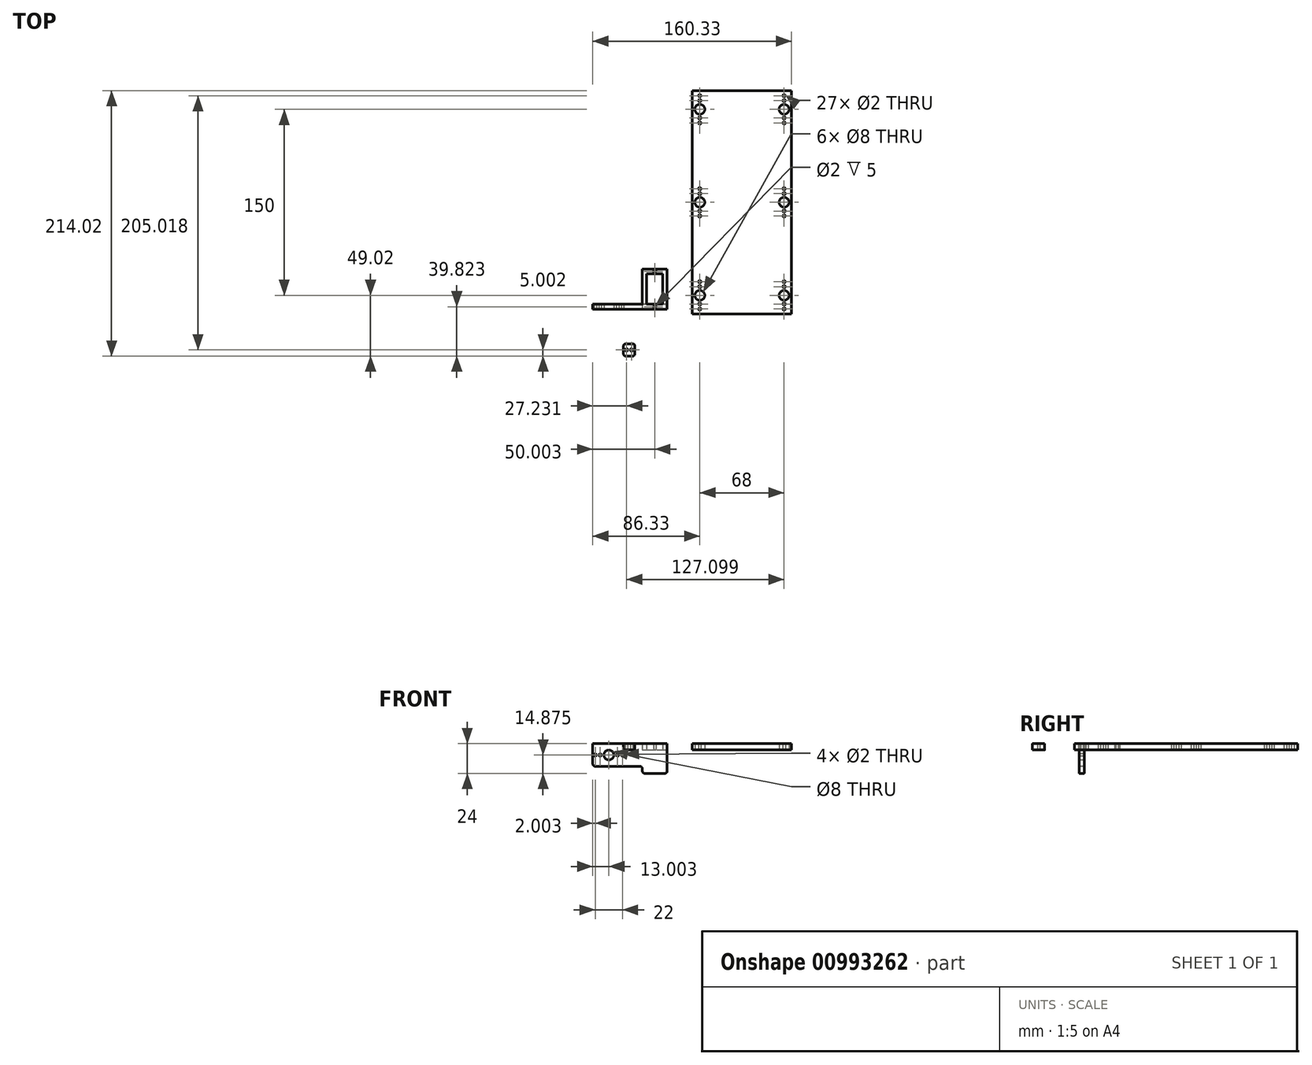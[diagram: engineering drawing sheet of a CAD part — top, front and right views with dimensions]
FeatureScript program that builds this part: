
annotation { "Feature Type Name" : "Feature", "Feature Type Description" : "" }
export const myFeature = defineFeature(function(context is Context, id is Id, definition is map)
    precondition{}
    {
        {
            var Q0;
            Q0=qCreatedBy(makeId("Top.planeOp"),FACE);
            var sketch = newSketch(context, id + "F0", { "sketchPlane" : qUnion([Q0])});
            skLineSegment(sketch, "E0.bottom", {"start": v(-36.83, 32.3) * mm, "end": v(-23.83, 32.3) * mm});
            skLineSegment(sketch, "E0.top", {"start": v(-36.83, 7.8) * mm, "end": v(-23.83, 7.8) * mm});
            skLineSegment(sketch, "E0.left", {"start": v(-36.83, 32.3) * mm, "end": v(-36.83, 7.8) * mm});
            skLineSegment(sketch, "E0.right", {"start": v(-23.83, 32.3) * mm, "end": v(-23.83, 7.8) * mm});
            skLineSegment(sketch, "E1.bottom", {"start": v(-40.33, 36.3) * mm, "end": v(-20.33, 36.3) * mm});
            skLineSegment(sketch, "E1.top", {"start": v(-40.33, 3.8) * mm, "end": v(-20.33, 3.8) * mm});
            skLineSegment(sketch, "E1.left", {"start": v(-40.33, 36.3) * mm, "end": v(-40.33, 3.8) * mm});
            skLineSegment(sketch, "E1.right", {"start": v(-20.33, 36.3) * mm, "end": v(-20.33, 3.8) * mm});
            skCircle(sketch, "E2", {"center": v(-30.33, 34.3) * mm, "radius": 1 * mm});
            skCircle(sketch, "E3", {"center": v(-30.33, 5.8) * mm, "radius": 1 * mm});
            skSolve(sketch);
        }
        {
            var Q0;
            Q0=makeQuery(id+"F0.imprint","IMPRINT",FACE,{"disambiguationData":[TD([[makeQuery(id+"F0.imprint","IMPRINT",EDGE,{"derivedFrom":sQuery(id+"F0.wireOp",EDGE,"E0.bottom")}),1.0]])]});
            extrude(context, id + "F1", {"entities" : qUnion([Q0]), "depth" : 5 * mm, "offsetDistance" : 25 * mm});
        }
        {
            var Q0;
            Q0=makeQuery(id+"F1.opExtrude","SWEPT_FACE",FACE,{"disambiguationData":[OSD([sQuery(id+"F0.wireOp",EDGE,"E1.top")])]});
            var sketch = newSketch(context, id + "F2", { "sketchPlane" : qUnion([Q0])});
            skLineSegment(sketch, "E4.bottom", {"start": v(-40.33, 0) * mm, "end": v(-20.33, 0) * mm});
            skLineSegment(sketch, "E4.top", {"start": v(-40.33, -19) * mm, "end": v(-20.33, -19) * mm});
            skLineSegment(sketch, "E4.left", {"start": v(-40.33, 5) * mm, "end": v(-40.33, 0) * mm});
            skLineSegment(sketch, "E4.right", {"start": v(-20.33, 0) * mm, "end": v(-20.33, -19) * mm});
            skLineSegment(sketch, "E5.bottom", {"start": v(-40.33, 5) * mm, "end": v(-80.33, 5) * mm});
            skLineSegment(sketch, "E5.top", {"start": v(-40.33, -13.25) * mm, "end": v(-80.33, -13.25) * mm});
            skLineSegment(sketch, "E5.right", {"start": v(-80.33, 5) * mm, "end": v(-80.33, -13.25) * mm});
            skLineSegment(sketch, "E6.trimOffspring", {"start": v(-40.33, -13.25) * mm, "end": v(-40.33, -19) * mm});
            skCircle(sketch, "E7", {"center": v(-78.33, -4.13) * mm, "radius": 1 * mm});
            skCircle(sketch, "E8", {"center": v(-74.33, -4.13) * mm, "radius": 1 * mm});
            skCircle(sketch, "E9", {"center": v(-67.33, -4.13) * mm, "radius": 4 * mm});
            skCircle(sketch, "E10", {"center": v(-60.33, -4.13) * mm, "radius": 1 * mm});
            skCircle(sketch, "E11", {"center": v(-56.33, -4.13) * mm, "radius": 1 * mm});
            skSolve(sketch);
        }
        {
            var Q0;
            Q0=makeQuery(id+"F2.imprint","IMPRINT",FACE,{"disambiguationData":[TD([[makeQuery(id+"F2.imprint","IMPRINT",EDGE,{"derivedFrom":sQuery(id+"F2.wireOp",EDGE,"E4.bottom")}),-1.0]])]});
            extrude(context, id + "F3", {"entities" : qUnion([Q0]), "operationType" : NewBodyOperationType.ADD, "oppositeDirection" : true, "depth" : 4 * mm, "offsetDistance" : 25 * mm});
        }
        {
            var Q0;
            Q0=makeQuery(id+"F3.opExtrude","SWEPT_EDGE",EDGE,{"disambiguationData":[OSD([sQuery(id+"F2.wireOp",EDGE,"E4.left"),sQuery(id+"F2.wireOp",EDGE,"E5.bottom")])]});
            var Q1;
            Q1=makeQuery(id+"F3.opExtrude","SWEPT_EDGE",EDGE,{"disambiguationData":[OSD([sQuery(id+"F2.wireOp",EDGE,"E5.top"),sQuery(id+"F2.wireOp",EDGE,"E6.trimOffspring")])]});
            var Q2;
            Q2=makeQuery(id+"F3.opExtrude","SWEPT_EDGE",EDGE,{"disambiguationData":[OSD([sQuery(id+"F2.wireOp",EDGE,"E4.top"),sQuery(id+"F2.wireOp",EDGE,"E6.trimOffspring")])]});
            var Q3;
            Q3=makeQuery(id+"F3.opExtrude","SWEPT_EDGE",EDGE,{"disambiguationData":[OSD([sQuery(id+"F2.wireOp",EDGE,"E4.top"),sQuery(id+"F2.wireOp",EDGE,"E4.right")])]});
            var Q4;
            Q4=makeQuery(id+"F3.opExtrude","SWEPT_EDGE",EDGE,{"disambiguationData":[OSD([sQuery(id+"F2.wireOp",EDGE,"E5.top"),sQuery(id+"F2.wireOp",EDGE,"E5.right")])]});
            fillet(context, id + "F4", {"entities" : qUnion([Q0, Q1, Q2, Q3, Q4]), "radius" : 2 * mm, "tangentPropagation" : true, "allowEdgeOverflow" : false});
        }
        {
            var Q0;
            Q0=qCreatedBy(makeId("Top.planeOp"),FACE);
            var sketch = newSketch(context, id + "F5", { "sketchPlane" : qUnion([Q0])});
            skLineSegment(sketch, "E12.bottom", {"start": v(-55.6, -24.02) * mm, "end": v(-46.34, -24.02) * mm});
            skLineSegment(sketch, "E12.top", {"start": v(-55.6, -34.02) * mm, "end": v(-46.34, -34.02) * mm});
            skLineSegment(sketch, "E12.left", {"start": v(-55.6, -24.02) * mm, "end": v(-55.6, -34.02) * mm});
            skLineSegment(sketch, "E12.right", {"start": v(-46.34, -24.02) * mm, "end": v(-46.34, -34.02) * mm});
            skCircle(sketch, "E13", {"center": v(-53.1, -29.02) * mm, "radius": 1 * mm});
            skCircle(sketch, "E14", {"center": v(-49.1, -29.02) * mm, "radius": 1 * mm});
            skSolve(sketch);
        }
        {
            var Q0;
            Q0=makeQuery(id+"F5.imprint","IMPRINT",FACE,{"disambiguationData":[TD([[makeQuery(id+"F5.imprint","IMPRINT",EDGE,{"derivedFrom":sQuery(id+"F5.wireOp",EDGE,"E12.bottom")}),-1.0]])]});
            extrude(context, id + "F6", {"entities" : qUnion([Q0]), "depth" : 5 * mm, "offsetDistance" : 25 * mm});
        }
        {
            var Q0;
            Q0=makeQuery(id+"F6.opExtrude","SWEPT_EDGE",EDGE,{"disambiguationData":[OSD([sQuery(id+"F5.wireOp",EDGE,"E12.bottom"),sQuery(id+"F5.wireOp",EDGE,"E12.left")])]});
            var Q1;
            Q1=makeQuery(id+"F6.opExtrude","SWEPT_EDGE",EDGE,{"disambiguationData":[OSD([sQuery(id+"F5.wireOp",EDGE,"E12.bottom"),sQuery(id+"F5.wireOp",EDGE,"E12.right")])]});
            var Q2;
            Q2=makeQuery(id+"F6.opExtrude","SWEPT_EDGE",EDGE,{"disambiguationData":[OSD([sQuery(id+"F5.wireOp",EDGE,"E12.top"),sQuery(id+"F5.wireOp",EDGE,"E12.left")])]});
            var Q3;
            Q3=makeQuery(id+"F6.opExtrude","SWEPT_EDGE",EDGE,{"disambiguationData":[OSD([sQuery(id+"F5.wireOp",EDGE,"E12.top"),sQuery(id+"F5.wireOp",EDGE,"E12.right")])]});
            fillet(context, id + "F7", {"entities" : qUnion([Q0, Q1, Q2, Q3]), "radius" : 2 * mm, "tangentPropagation" : true, "allowEdgeOverflow" : false});
        }
        {
            var Q0;
            Q0=qCreatedBy(makeId("Top.planeOp"),FACE);
            var sketch = newSketch(context, id + "F8", { "sketchPlane" : qUnion([Q0])});
            skLineSegment(sketch, "E15.bottom", {"start": v(0, 180) * mm, "end": v(80, 180) * mm});
            skLineSegment(sketch, "E15.top", {"start": v(0, 0) * mm, "end": v(80, 0) * mm});
            skLineSegment(sketch, "E15.left", {"start": v(0, 180) * mm, "end": v(0, 0) * mm});
            skLineSegment(sketch, "E15.right", {"start": v(80, 180) * mm, "end": v(80, 0) * mm});
            skCircle(sketch, "E16", {"center": v(6, 4) * mm, "radius": 1 * mm});
            skCircle(sketch, "E17", {"center": v(6, 8) * mm, "radius": 1 * mm});
            skCircle(sketch, "E18", {"center": v(6, 15) * mm, "radius": 4 * mm});
            skCircle(sketch, "E19", {"center": v(6, 22) * mm, "radius": 1 * mm});
            skCircle(sketch, "E20", {"center": v(6, 26) * mm, "radius": 1 * mm});
            skCircle(sketch, "E21", {"center": v(6, 154) * mm, "radius": 1 * mm});
            skCircle(sketch, "E22", {"center": v(6, 158) * mm, "radius": 1 * mm});
            skCircle(sketch, "E23", {"center": v(6, 165) * mm, "radius": 4 * mm});
            skCircle(sketch, "E24", {"center": v(6, 172) * mm, "radius": 1 * mm});
            skCircle(sketch, "E25", {"center": v(6, 176) * mm, "radius": 1 * mm});
            skCircle(sketch, "E26", {"center": v(6, 79) * mm, "radius": 1 * mm});
            skCircle(sketch, "E27", {"center": v(6, 83) * mm, "radius": 1 * mm});
            skCircle(sketch, "E28", {"center": v(6, 90) * mm, "radius": 4 * mm});
            skCircle(sketch, "E29", {"center": v(6, 97) * mm, "radius": 1 * mm});
            skCircle(sketch, "E30", {"center": v(6, 101) * mm, "radius": 1 * mm});
            skCircle(sketch, "E31", {"center": v(74, 4) * mm, "radius": 1 * mm});
            skCircle(sketch, "E32", {"center": v(74, 8) * mm, "radius": 1 * mm});
            skCircle(sketch, "E33", {"center": v(74, 15) * mm, "radius": 4 * mm});
            skCircle(sketch, "E34", {"center": v(74, 22) * mm, "radius": 1 * mm});
            skCircle(sketch, "E35", {"center": v(74, 26) * mm, "radius": 1 * mm});
            skCircle(sketch, "E36", {"center": v(74, 154) * mm, "radius": 1 * mm});
            skCircle(sketch, "E37", {"center": v(74, 158) * mm, "radius": 1 * mm});
            skCircle(sketch, "E38", {"center": v(74, 165) * mm, "radius": 4 * mm});
            skCircle(sketch, "E39", {"center": v(74, 172) * mm, "radius": 1 * mm});
            skCircle(sketch, "E40", {"center": v(74, 176) * mm, "radius": 1 * mm});
            skCircle(sketch, "E41", {"center": v(74, 79) * mm, "radius": 1 * mm});
            skCircle(sketch, "E42", {"center": v(74, 83) * mm, "radius": 1 * mm});
            skCircle(sketch, "E43", {"center": v(74, 90) * mm, "radius": 4 * mm});
            skCircle(sketch, "E44", {"center": v(74, 97) * mm, "radius": 1 * mm});
            skCircle(sketch, "E45", {"center": v(74, 101) * mm, "radius": 1 * mm});
            skSolve(sketch);
        }
        {
            var Q0;
            Q0=makeQuery(id+"F8.imprint","IMPRINT",FACE,{"disambiguationData":[TD([[makeQuery(id+"F8.imprint","IMPRINT",EDGE,{"derivedFrom":sQuery(id+"F8.wireOp",EDGE,"E15.bottom")}),-1.0]])]});
            extrude(context, id + "F9", {"entities" : qUnion([Q0]), "depth" : 5 * mm, "offsetDistance" : 25 * mm});
        }
    });
